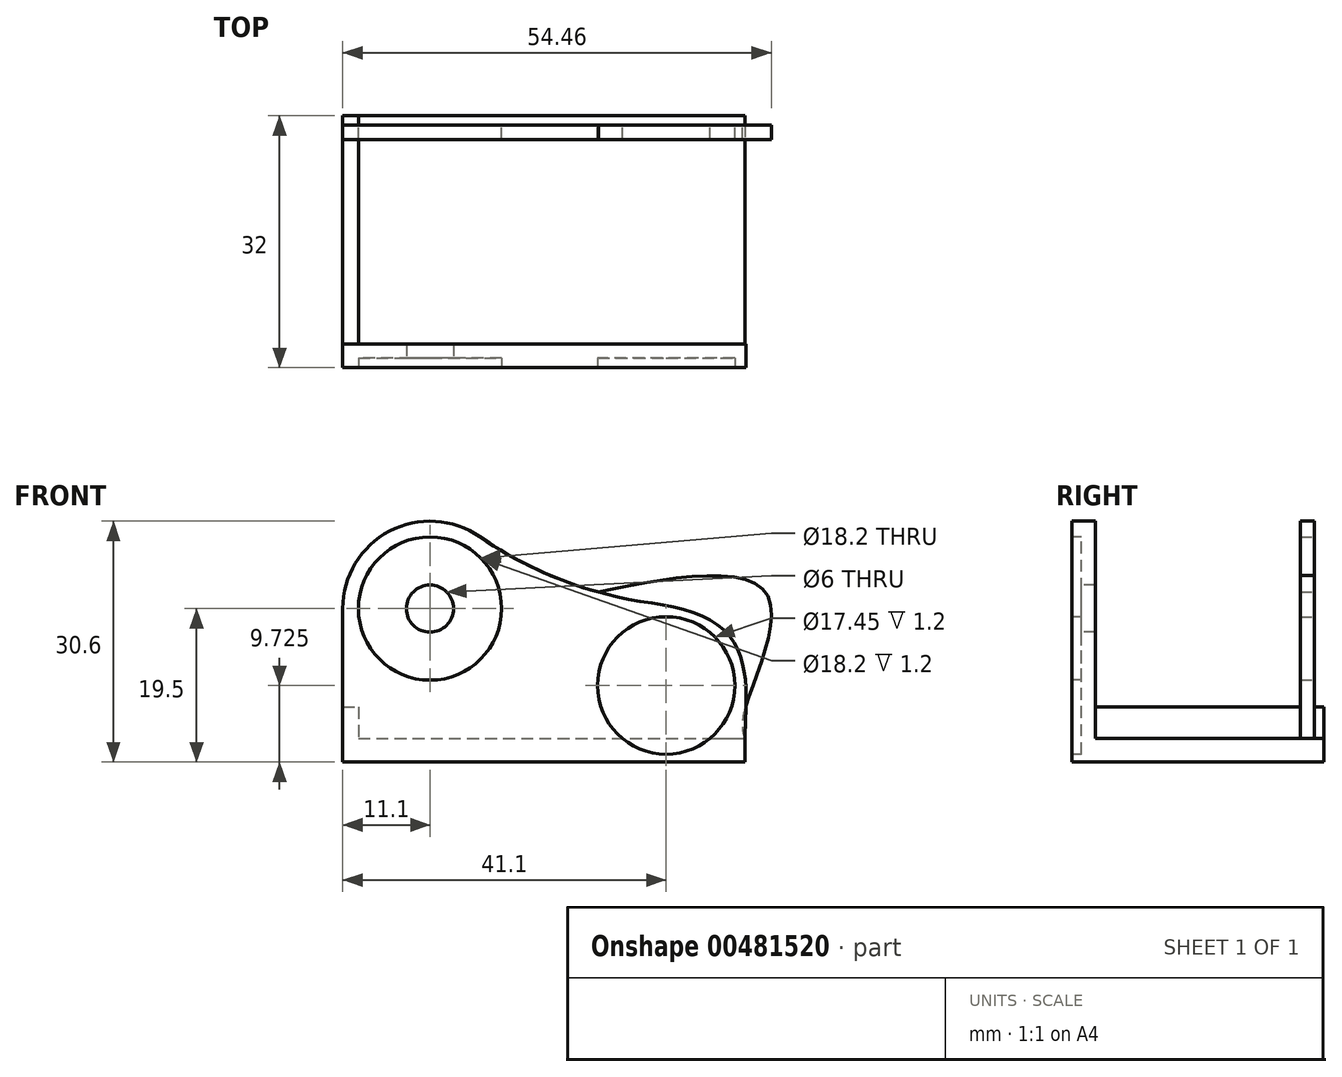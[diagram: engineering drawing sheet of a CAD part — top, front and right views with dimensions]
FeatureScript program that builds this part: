
annotation { "Feature Type Name" : "Feature", "Feature Type Description" : "" }
export const myFeature = defineFeature(function(context is Context, id is Id, definition is map)
    precondition{}
    {
        {
            var Q0;
            Q0=qCreatedBy(makeId("Front.planeOp"),FACE);
            var sketch = newSketch(context, id + "F0", { "sketchPlane" : qUnion([Q0])});
            skLineSegment(sketch, "E0.bottom", {"start": v(0, 0) * mm, "end": v(51.1, 0) * mm});
            skLineSegment(sketch, "E0.top", {"start": v(0, 3) * mm, "end": v(51.1, 3) * mm});
            skLineSegment(sketch, "E0.left", {"start": v(0, 0) * mm, "end": v(0, 3) * mm});
            skLineSegment(sketch, "E0.right", {"start": v(51.1, 0) * mm, "end": v(51.1, 3) * mm});
            skCircle(sketch, "E1", {"center": v(11.1, 19.5) * mm, "radius": 3 * mm});
            skCircle(sketch, "E2", {"center": v(11.1, 19.5) * mm, "radius": 9.1 * mm});
            skLineSegment(sketch, "E3", {"start": v(0, 3) * mm, "end": v(0, 19.5) * mm});
            skArc(sketch, "E4", {"start": v(17.4, 28.63) * mm, "mid": v(5.94, 29.33) * mm, "end": v(0, 19.5) * mm});
            skFitSpline(sketch, "E5", {"points": [v(22.2, 19.5) * mm, v(48.73, 16.46) * mm, v(51.1, 3) * mm], "startDerivative": vector(42.05, 8.29) * mm, "endDerivative": vector(0, -25.99) * mm});
            skArc(sketch, "E6.filletArc", {"start": v(17.4, 28.63) * mm, "mid": v(27.84, 23.12) * mm, "end": v(39.27, 20.2) * mm});
            skCircle(sketch, "E7", {"center": v(41.1, 9.73) * mm, "radius": 8.72 * mm});
            skLineSegment(sketch, "E8", {"start": v(0, 7) * mm, "end": v(2, 7) * mm});
            skLineSegment(sketch, "E9", {"start": v(2, 7) * mm, "end": v(2, 3) * mm});
            skSolve(sketch);
        }
        {
            var Q0;
            Q0=makeQuery(id+"F0.imprint","IMPRINT",FACE,{"disambiguationData":[TD([[makeQuery(id+"F0.imprint","IMPRINT",EDGE,{"derivedFrom":sQuery(id+"F0.wireOp",EDGE,"E2")}),-1.0]])]});
            var Q1;
            {var subQ4=sQuery(id+"F0.wireOp",EDGE,"E8");Q1=makeQuery(id+"F0.imprint","IMPRINT",FACE,{"disambiguationData":[TD([[makeQuery(id+"F0.imprint","IMPRINT",EDGE,{"derivedFrom":subQ4}),-1.0]])]});}
            var Q2;
            Q2=makeQuery(id+"F0.imprint","IMPRINT",FACE,{"disambiguationData":[TD([[makeQuery(id+"F0.imprint","IMPRINT",EDGE,{"derivedFrom":sQuery(id+"F0.wireOp",EDGE,"E0.bottom")}),1.0]])]});
            var Q3;
            {var subQ0=sQuery(id+"F0.wireOp",EDGE,"E7");var subQ1=sQuery(id+"F0.wireOp",EDGE,"E0.top");var subQ2=makeQuery(id+"F0.imprint","INTERSECT",VERTEX,{"disambiguationData":[OD(0.0)],"derivedFrom":[subQ1,subQ0]});Q3=makeQuery(id+"F0.imprint","IMPRINT",FACE,{"disambiguationData":[TD([[makeQuery(id+"F0.imprint","IMPRINT",EDGE,{"disambiguationData":[TD([[subQ2,-1.0]])],"derivedFrom":subQ1}),1.0]])]});}
            var Q4;
            {var subQ0=sQuery(id+"F0.wireOp",EDGE,"E7");var subQ1=sQuery(id+"F0.wireOp",EDGE,"E0.top");var subQ2=makeQuery(id+"F0.imprint","INTERSECT",VERTEX,{"disambiguationData":[OD(0.0)],"derivedFrom":[subQ1,subQ0]});Q4=makeQuery(id+"F0.imprint","IMPRINT",FACE,{"disambiguationData":[TD([[makeQuery(id+"F0.imprint","IMPRINT",EDGE,{"disambiguationData":[TD([[subQ2,-1.0]])],"derivedFrom":subQ1}),-1.0]])]});}
            var Q5;
            Q5=makeQuery(id+"F0.imprint","IMPRINT",FACE,{"disambiguationData":[TD([[makeQuery(id+"F0.imprint","IMPRINT",EDGE,{"derivedFrom":sQuery(id+"F0.wireOp",EDGE,"E1")}),-1.0]])]});
            extrude(context, id + "F1", {"entities" : qUnion([Q0, Q1, Q2, Q3, Q4, Q5]), "oppositeDirection" : true, "depth" : 3 * mm, "offsetDistance" : 25 * mm});
        }
        {
            var Q0;
            {var subQ0=sQuery(id+"F0.wireOp",EDGE,"E7");var subQ1=sQuery(id+"F0.wireOp",EDGE,"E0.top");var subQ2=makeQuery(id+"F0.imprint","INTERSECT",VERTEX,{"disambiguationData":[OD(0.0)],"derivedFrom":[subQ1,subQ0]});Q0=makeQuery(id+"F0.imprint","IMPRINT",FACE,{"disambiguationData":[TD([[makeQuery(id+"F0.imprint","IMPRINT",EDGE,{"disambiguationData":[TD([[subQ2,-1.0]])],"derivedFrom":subQ1}),-1.0]])]});}
            var Q1;
            Q1=makeQuery(id+"F0.imprint","IMPRINT",FACE,{"disambiguationData":[TD([[makeQuery(id+"F0.imprint","IMPRINT",EDGE,{"derivedFrom":sQuery(id+"F0.wireOp",EDGE,"E0.bottom")}),1.0]])]});
            var Q2;
            {var subQ4=sQuery(id+"F0.wireOp",EDGE,"E8");Q2=makeQuery(id+"F0.imprint","IMPRINT",FACE,{"disambiguationData":[TD([[makeQuery(id+"F0.imprint","IMPRINT",EDGE,{"derivedFrom":subQ4}),-1.0]])]});}
            extrude(context, id + "F2", {"entities" : qUnion([Q0, Q1, Q2]), "operationType" : NewBodyOperationType.ADD, "oppositeDirection" : true, "depth" : 32 * mm, "offsetDistance" : 25 * mm});
        }
        {
            var Q0;
            Q0=makeQuery(id+"F2.opExtrude","CAP_FACE",FACE,{"disambiguationData":[OSD([sQuery(id+"F0.wireOp",EDGE,"E0.bottom"),sQuery(id+"F0.wireOp",EDGE,"E0.top"),sQuery(id+"F0.wireOp",EDGE,"E0.left"),sQuery(id+"F0.wireOp",EDGE,"E0.right"),sQuery(id+"F0.wireOp",EDGE,"E3"),sQuery(id+"F0.wireOp",EDGE,"E8"),sQuery(id+"F0.wireOp",EDGE,"E9")])],"isStart":false});
            var sketch = newSketch(context, id + "F3", { "sketchPlane" : qUnion([Q0])});
            skLineSegment(sketch, "E10.0.0", {"start": v(-2, 3) * mm, "end": v(-35.54, 3) * mm});
            skArc(sketch, "E10.0.1", {"start": v(-35.54, 3) * mm, "mid": v(-41.1, 18.45) * mm, "end": v(-46.66, 3) * mm});
            skLineSegment(sketch, "E10.0.2", {"start": v(-46.66, 3) * mm, "end": v(-51.1, 3) * mm});
            skFitSpline(sketch, "E10.0.3", {"points": [v(-51.1, 3) * mm, v(-51.1, 6.61) * mm, v(-53.65, 21.68) * mm, v(-30.37, 21.11) * mm, v(-22.2, 19.5) * mm]});
            skArc(sketch, "E10.0.4", {"start": v(-39.27, 20.2) * mm, "mid": v(-27.84, 23.12) * mm, "end": v(-17.4, 28.63) * mm});
            skArc(sketch, "E10.0.5", {"start": v(-17.4, 28.63) * mm, "mid": v(-5.94, 29.33) * mm, "end": v(0, 19.5) * mm});
            skLineSegment(sketch, "E10.0.6", {"start": v(0, 19.5) * mm, "end": v(0, 7) * mm});
            skLineSegment(sketch, "E10.0.7", {"start": v(0, 7) * mm, "end": v(-2, 7) * mm});
            skLineSegment(sketch, "E10.0.8", {"start": v(-2, 7) * mm, "end": v(-2, 3) * mm});
            skCircle(sketch, "E10.1.0", {"center": v(-11.1, 19.5) * mm, "radius": 9.1 * mm});
            skArc(sketch, "E10.2.0", {"start": v(-46.66, 3) * mm, "mid": v(-41.1, 18.45) * mm, "end": v(-35.54, 3) * mm});
            skLineSegment(sketch, "E10.2.1", {"start": v(-35.54, 3) * mm, "end": v(-46.66, 3) * mm});
            skCircle(sketch, "E11.0", {"center": v(-11.1, 19.5) * mm, "radius": 3 * mm});
            skSolve(sketch);
        }
        {
            var Q0;
            Q0=makeQuery(id+"F3.imprint","IMPRINT",FACE,{"disambiguationData":[TD([[makeQuery(id+"F3.imprint","IMPRINT",EDGE,{"derivedFrom":sQuery(id+"F3.wireOp",EDGE,"E10.0.0")}),-1.0]])]});
            var Q1;
            Q1=makeQuery(id+"F3.imprint","IMPRINT",FACE,{"disambiguationData":[TD([[makeQuery(id+"F3.imprint","IMPRINT",EDGE,{"derivedFrom":sQuery(id+"F3.wireOp",EDGE,"E10.2.0")}),-1.0]])]});
            var Q2;
            Q2=makeQuery(id+"F3.imprint","IMPRINT",FACE,{"disambiguationData":[TD([[makeQuery(id+"F3.imprint","IMPRINT",EDGE,{"derivedFrom":sQuery(id+"F3.wireOp",EDGE,"E10.1.0")}),-1.0]])]});
            extrude(context, id + "F4", {"entities" : qUnion([Q0, Q1, Q2]), "operationType" : NewBodyOperationType.ADD, "oppositeDirection" : true, "depth" : 3 * mm, "offsetDistance" : 25 * mm});
        }
        {
            var Q0;
            Q0=makeQuery(id+"F0.imprint","IMPRINT",FACE,{"disambiguationData":[TD([[makeQuery(id+"F0.imprint","IMPRINT",EDGE,{"derivedFrom":sQuery(id+"F0.wireOp",EDGE,"E1")}),-1.0]])]});
            var Q1;
            {var subQ0=sQuery(id+"F0.wireOp",EDGE,"E7");var subQ1=sQuery(id+"F0.wireOp",EDGE,"E0.top");var subQ2=makeQuery(id+"F0.imprint","INTERSECT",VERTEX,{"disambiguationData":[OD(0.0)],"derivedFrom":[subQ1,subQ0]});Q1=makeQuery(id+"F0.imprint","IMPRINT",FACE,{"disambiguationData":[TD([[makeQuery(id+"F0.imprint","IMPRINT",EDGE,{"disambiguationData":[TD([[subQ2,-1.0]])],"derivedFrom":subQ1}),1.0]])]});}
            var Q2;
            {var subQ0=sQuery(id+"F0.wireOp",EDGE,"E7");var subQ1=sQuery(id+"F0.wireOp",EDGE,"E0.top");var subQ2=makeQuery(id+"F0.imprint","INTERSECT",VERTEX,{"disambiguationData":[OD(0.0)],"derivedFrom":[subQ1,subQ0]});Q2=makeQuery(id+"F0.imprint","IMPRINT",FACE,{"disambiguationData":[TD([[makeQuery(id+"F0.imprint","IMPRINT",EDGE,{"disambiguationData":[TD([[subQ2,-1.0]])],"derivedFrom":subQ1}),-1.0]])]});}
            extrude(context, id + "F5", {"entities" : qUnion([Q0, Q1, Q2]), "operationType" : NewBodyOperationType.REMOVE, "oppositeDirection" : true, "depth" : 1.2 * mm, "offsetDistance" : 25 * mm});
        }
        {
            var Q0;
            Q0=makeQuery(id+"F3.imprint","IMPRINT",FACE,{"disambiguationData":[TD([[makeQuery(id+"F3.imprint","IMPRINT",EDGE,{"derivedFrom":sQuery(id+"F3.wireOp",EDGE,"E10.1.0")}),-1.0]])]});
            extrude(context, id + "F6", {"entities" : qUnion([Q0]), "operationType" : NewBodyOperationType.REMOVE, "oppositeDirection" : true, "depth" : 1.2 * mm, "offsetDistance" : 25 * mm});
        }
    });
